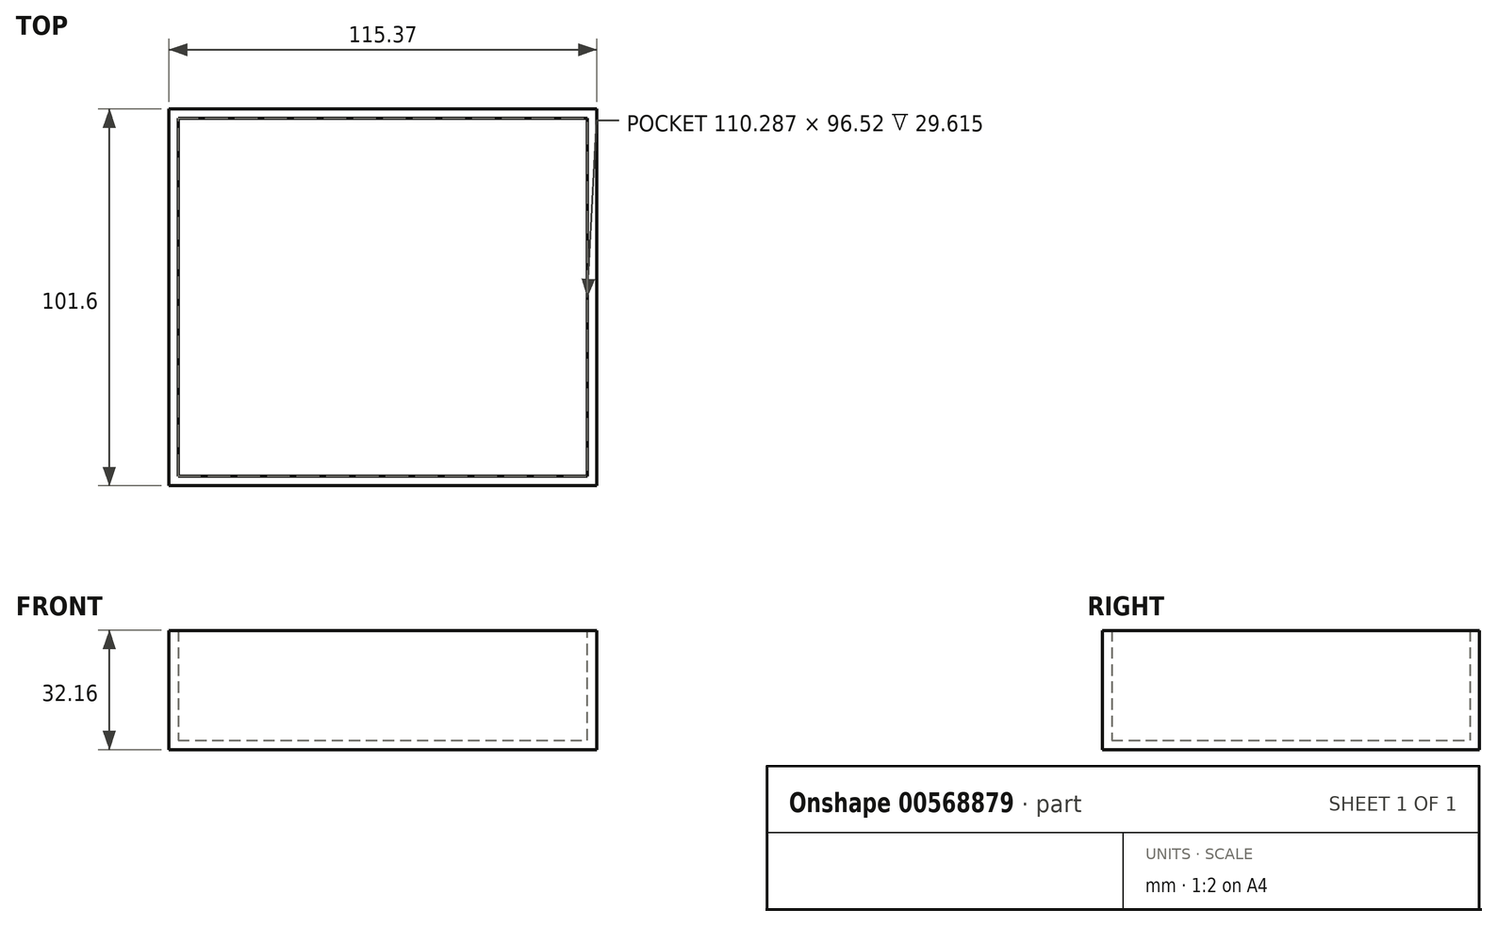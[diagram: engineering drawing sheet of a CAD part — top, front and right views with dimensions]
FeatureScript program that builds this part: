
annotation { "Feature Type Name" : "Feature", "Feature Type Description" : "" }
export const myFeature = defineFeature(function(context is Context, id is Id, definition is map)
    precondition{}
    {
        {
            var Q0;
            Q0=qCreatedBy(makeId("Front.planeOp"),FACE);
            var sketch = newSketch(context, id + "F0", { "sketchPlane" : qUnion([Q0])});
            skLineSegment(sketch, "E0", {"start": v(-44.39, 32.16) * mm, "end": v(70.98, 32.16) * mm});
            skLineSegment(sketch, "E1", {"start": v(-44.39, 32.16) * mm, "end": v(-44.39, 0) * mm});
            skLineSegment(sketch, "E2", {"start": v(-44.39, 0) * mm, "end": v(70.98, 0) * mm});
            skLineSegment(sketch, "E3", {"start": v(70.98, 0) * mm, "end": v(70.98, 32.16) * mm});
            skSolve(sketch);
        }
        {
            var Q0;
            Q0=makeQuery(id+"F0.imprint","IMPRINT",FACE,{"disambiguationData":[TD([[makeQuery(id+"F0.imprint","IMPRINT",EDGE,{"derivedFrom":sQuery(id+"F0.wireOp",EDGE,"E0")}),-1.0]])]});
            extrude(context, id + "F1", {"entities" : qUnion([Q0]), "depth" : 101.6 * mm, "offsetDistance" : 25.4 * mm});
        }
        {
            var Q0;
            Q0=makeQuery(id+"F1.opExtrude","SWEPT_FACE",FACE,{"disambiguationData":[OSD([sQuery(id+"F0.wireOp",EDGE,"E0")])]});
            shell(context, id + "F2", {"entities" : qUnion([Q0]), "thickness" : 2.54 * mm});
        }
    });
